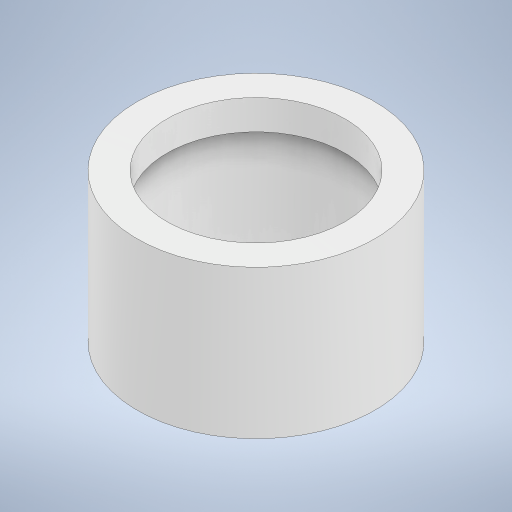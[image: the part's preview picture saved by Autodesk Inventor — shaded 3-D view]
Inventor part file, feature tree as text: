
AUTODESK INVENTOR PART (.ipt)
format: ipt  version: 2023 (Build 270158000, 158)  size: 233,984 bytes
history: native  units: mm
features: extrude x2, sketch x2
ambient origin geometry x8: Origin, YZ Plane, XZ Plane, XY Plane, X Axis, Y Axis, Z Axis, Center Point
bodies: Solid1 (feature_tree)
feature tree (4):
  extrude  "Extrusion1"  Depth=10.0mm
  extrude  "Extrusion2"  Depth=10.0mm
  sketch  "Sketch1"  dims[d0=160.0mm d1=10.0mm]
  sketch  "Sketch2"  dims[d2=100.0mm d3=0.0mm d4=10.0mm d5=20.0mm d6=0.0mm]
